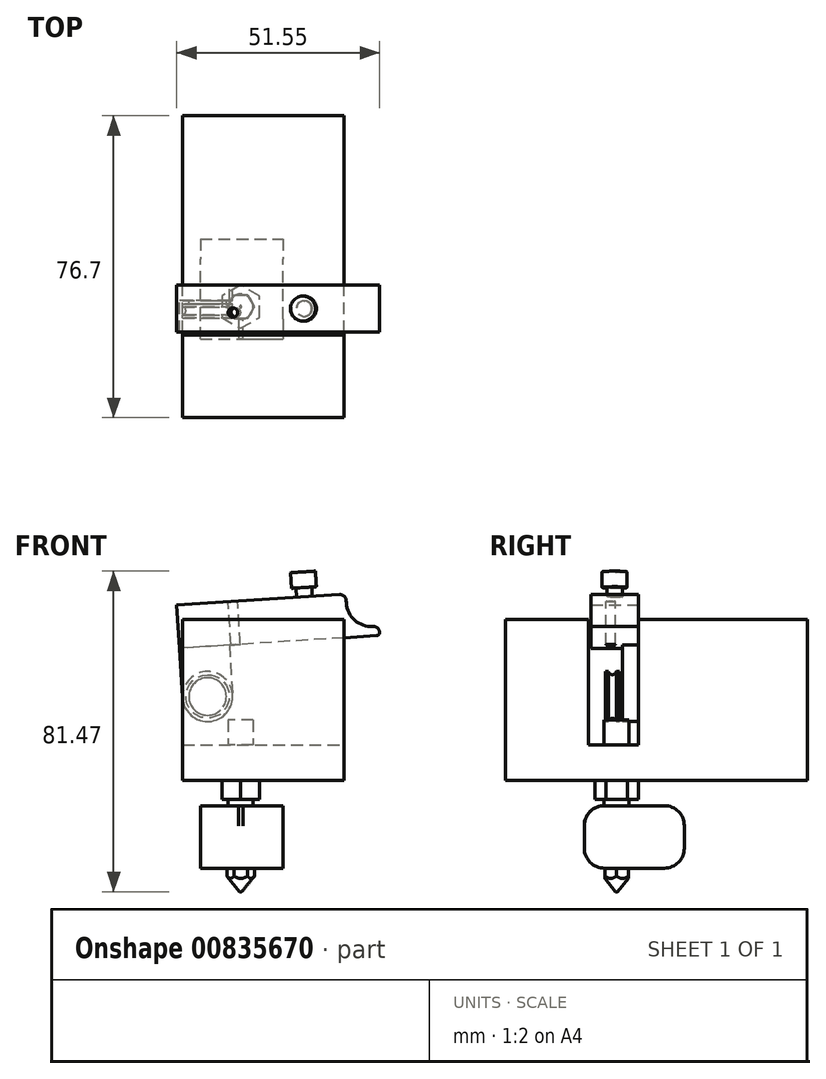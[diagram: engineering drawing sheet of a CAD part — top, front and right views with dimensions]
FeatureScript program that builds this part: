
annotation { "Feature Type Name" : "Feature", "Feature Type Description" : "" }
export const myFeature = defineFeature(function(context is Context, id is Id, definition is map)
    precondition{}
    {
        {
            var Q0;
            Q0=qCreatedBy(makeId("Front.planeOp"),FACE);
            var sketch = newSketch(context, id + "F0", { "sketchPlane" : qUnion([Q0])});
            skLineSegment(sketch, "E0.bottom", {"start": v(-20.5, 20.5) * mm, "end": v(20.5, 20.5) * mm});
            skLineSegment(sketch, "E0.top", {"start": v(-20.5, -20.5) * mm, "end": v(20.5, -20.5) * mm});
            skLineSegment(sketch, "E0.left", {"start": v(-20.5, 20.5) * mm, "end": v(-20.5, -20.5) * mm});
            skLineSegment(sketch, "E0.right", {"start": v(20.5, 20.5) * mm, "end": v(20.5, -20.5) * mm});
            skSolve(sketch);
        }
        {
            var Q0;
            Q0 = qSketchRegion(id + "F0", true);
            extrude(context, id + "F1", {"entities" : qUnion([Q0]), "depth" : 43 * mm, "offsetDistance" : 25.4 * mm});
        }
        {
            var Q0;
            Q0=makeQuery(id+"F1.opExtrude","CAP_FACE",FACE,{"disambiguationData":[OSD([sQuery(id+"F0.wireOp",EDGE,"E0.bottom"),sQuery(id+"F0.wireOp",EDGE,"E0.top"),sQuery(id+"F0.wireOp",EDGE,"E0.left"),sQuery(id+"F0.wireOp",EDGE,"E0.right")])],"isStart":false});
            var sketch = newSketch(context, id + "F2", { "sketchPlane" : qUnion([Q0])});
            skLineSegment(sketch, "E1.bottom", {"start": v(-20.5, -11.5) * mm, "end": v(20.5, -11.5) * mm});
            skLineSegment(sketch, "E1.top", {"start": v(-20.5, -20.5) * mm, "end": v(20.5, -20.5) * mm});
            skLineSegment(sketch, "E1.left", {"start": v(-20.5, -11.5) * mm, "end": v(-20.5, -20.5) * mm});
            skLineSegment(sketch, "E1.right", {"start": v(20.5, -11.5) * mm, "end": v(20.5, -20.5) * mm});
            skSolve(sketch);
        }
        {
            var Q0;
            Q0 = qSketchRegion(id + "F2", true);
            extrude(context, id + "F3", {"entities" : qUnion([Q0]), "operationType" : NewBodyOperationType.ADD, "depth" : 12.7 * mm, "offsetDistance" : 25.4 * mm});
        }
        {
            var Q0;
            Q0=makeQuery(id+"F1.opExtrude","CAP_FACE",FACE,{"disambiguationData":[OSD([sQuery(id+"F0.wireOp",EDGE,"E0.bottom"),sQuery(id+"F0.wireOp",EDGE,"E0.top"),sQuery(id+"F0.wireOp",EDGE,"E0.left"),sQuery(id+"F0.wireOp",EDGE,"E0.right")])],"isStart":false});
            var sketch = newSketch(context, id + "F4", { "sketchPlane" : qUnion([Q0])});
            skLineSegment(sketch, "E2", {"start": v(-20.49, 0.44) * mm, "end": v(-22, 24.1) * mm});
            skLineSegment(sketch, "E3", {"start": v(-22, 24.1) * mm, "end": v(20.96, 26.85) * mm});
            skLineSegment(sketch, "E4", {"start": v(20.96, 26.85) * mm, "end": v(21.5, 18.26) * mm});
            skLineSegment(sketch, "E5", {"start": v(21.5, 18.26) * mm, "end": v(29.44, 18.76) * mm});
            skLineSegment(sketch, "E6", {"start": v(29.44, 18.76) * mm, "end": v(29.6, 16.38) * mm});
            skLineSegment(sketch, "E7", {"start": v(29.6, 16.38) * mm, "end": v(-8.63, 13.93) * mm});
            skLineSegment(sketch, "E8", {"start": v(-8.63, 13.93) * mm, "end": v(-7.81, 1.26) * mm});
            skArc(sketch, "E9", {"start": v(-20.49, 0.44) * mm, "mid": v(-13.74, -5.49) * mm, "end": v(-7.81, 1.26) * mm});
            skSolve(sketch);
        }
        {
            var Q0;
            Q0 = qSketchRegion(id + "F4", true);
            extrude(context, id + "F5", {"entities" : qUnion([Q0]), "operationType" : NewBodyOperationType.ADD, "depth" : 4 * mm, "offsetDistance" : 25.4 * mm});
        }
        {
            var Q0;
            Q0=makeQuery(id+"F5.opExtrude","SWEPT_EDGE",EDGE,{"disambiguationData":[OSD([sQuery(id+"F4.wireOp",EDGE,"E4"),sQuery(id+"F4.wireOp",EDGE,"E5")])]});
            fillet(context, id + "F6", {"entities" : qUnion([Q0]), "radius" : 6.35 * mm, "tangentPropagation" : true, "allowEdgeOverflow" : false});
        }
        {
            var Q0;
            Q0=makeQuery(id+"F5.opExtrude","SWEPT_EDGE",EDGE,{"disambiguationData":[OSD([sQuery(id+"F4.wireOp",EDGE,"E5"),sQuery(id+"F4.wireOp",EDGE,"E6")])]});
            fillet(context, id + "F7", {"entities" : qUnion([Q0]), "radius" : 1.6 * mm, "tangentPropagation" : true, "allowEdgeOverflow" : false});
        }
        {
            var Q0;
            Q0=makeQuery(id+"F5.opExtrude","SWEPT_EDGE",EDGE,{"disambiguationData":[OSD([sQuery(id+"F4.wireOp",EDGE,"E3"),sQuery(id+"F4.wireOp",EDGE,"E4")])]});
            fillet(context, id + "F8", {"entities" : qUnion([Q0]), "radius" : 1.6 * mm, "tangentPropagation" : true, "allowEdgeOverflow" : false});
        }
        {
            var Q0;
            Q0=makeQuery(id+"F5.opExtrude","SWEPT_EDGE",EDGE,{"disambiguationData":[OSD([sQuery(id+"F4.wireOp",EDGE,"E6"),sQuery(id+"F4.wireOp",EDGE,"E7")])]});
            fillet(context, id + "F9", {"entities" : qUnion([Q0]), "radius" : 0.79 * mm, "tangentPropagation" : true, "allowEdgeOverflow" : false});
        }
        {
            var Q0;
            Q0=makeQuery(id+"F5.opExtrude","CAP_FACE",FACE,{"disambiguationData":[OSD([sQuery(id+"F4.wireOp",EDGE,"E2"),sQuery(id+"F4.wireOp",EDGE,"E3"),sQuery(id+"F4.wireOp",EDGE,"E4"),sQuery(id+"F4.wireOp",EDGE,"E5"),sQuery(id+"F4.wireOp",EDGE,"E6"),sQuery(id+"F4.wireOp",EDGE,"E7"),sQuery(id+"F4.wireOp",EDGE,"E8"),sQuery(id+"F4.wireOp",EDGE,"E9")])],"isStart":false});
            var sketch = newSketch(context, id + "F10", { "sketchPlane" : qUnion([Q0])});
            skLineSegment(sketch, "E10.0", {"start": v(-22, 24.1) * mm, "end": v(19.36, 26.75) * mm});
            skArc(sketch, "E10.1", {"start": v(21.06, 25.25) * mm, "mid": v(20.52, 26.35) * mm, "end": v(19.36, 26.75) * mm});
            skLineSegment(sketch, "E10.2", {"start": v(21.06, 25.25) * mm, "end": v(21.1, 24.6) * mm});
            skArc(sketch, "E10.3", {"start": v(27.85, 18.66) * mm, "mid": v(23.25, 20.23) * mm, "end": v(21.1, 24.6) * mm});
            skArc(sketch, "E10.4", {"start": v(29.55, 17.17) * mm, "mid": v(29, 18.27) * mm, "end": v(27.85, 18.66) * mm});
            skArc(sketch, "E10.5", {"start": v(28.8, 16.33) * mm, "mid": v(29.35, 16.6) * mm, "end": v(29.55, 17.17) * mm});
            skLineSegment(sketch, "E10.6", {"start": v(28.8, 16.33) * mm, "end": v(-8.63, 13.93) * mm});
            skLineSegment(sketch, "E11", {"start": v(-8.63, 13.93) * mm, "end": v(-21.3, 13.12) * mm});
            skLineSegment(sketch, "E12", {"start": v(-22, 24.1) * mm, "end": v(-21.3, 13.12) * mm});
            skSolve(sketch);
        }
        {
            var Q0;
            Q0 = qSketchRegion(id + "F10", true);
            extrude(context, id + "F11", {"entities" : qUnion([Q0]), "operationType" : NewBodyOperationType.ADD, "depth" : 8 * mm, "offsetDistance" : 25.4 * mm});
        }
        {
            var Q0;
            Q0=makeQuery(id+"F3.opExtrude","CAP_FACE",FACE,{"disambiguationData":[OSD([sQuery(id+"F2.wireOp",EDGE,"E1.bottom"),sQuery(id+"F2.wireOp",EDGE,"E1.top"),sQuery(id+"F2.wireOp",EDGE,"E1.left"),sQuery(id+"F2.wireOp",EDGE,"E1.right")])],"isStart":false});
            var sketch = newSketch(context, id + "F12", { "sketchPlane" : qUnion([Q0])});
            skLineSegment(sketch, "E13.0.0", {"start": v(-20.5, -20.5) * mm, "end": v(-20.5, 20.5) * mm});
            skLineSegment(sketch, "E13.0.1", {"start": v(-20.5, 20.5) * mm, "end": v(20.5, 20.5) * mm});
            skLineSegment(sketch, "E13.0.2", {"start": v(20.5, 20.5) * mm, "end": v(20.5, -20.5) * mm});
            skLineSegment(sketch, "E13.0.3", {"start": v(20.5, -20.5) * mm, "end": v(-20.5, -20.5) * mm});
            skSolve(sketch);
        }
        {
            var Q0;
            Q0 = qSketchRegion(id + "F12", true);
            extrude(context, id + "F13", {"entities" : qUnion([Q0]), "operationType" : NewBodyOperationType.ADD, "depth" : 21 * mm, "offsetDistance" : 25.4 * mm});
        }
        {
            var Q0;
            Q0=makeQuery(id+"F11.boolean.opBoolean","MERGE",FACE,{"derivedFrom":[makeQuery(id+"F5.opExtrude","SWEPT_FACE",FACE,{"disambiguationData":[OSD([sQuery(id+"F4.wireOp",EDGE,"E3")])]}),makeQuery(id+"F11.opExtrude","SWEPT_FACE",FACE,{"disambiguationData":[OSD([sQuery(id+"F10.wireOp",EDGE,"E10.0")])]})]});
            var sketch = newSketch(context, id + "F14", { "sketchPlane" : qUnion([Q0])});
            skPoint(sketch, "E14", {"position": v(-6.12, -50) * mm});
            skSolve(sketch);
        }
        {
            var Q0;
            Q0=sQuery(id+"F14.wireOp",VERTEX,"E14");
            var Q1;
            Q1=makeQuery(id+"F1.opExtrude","SWEPT_BODY",BODY,{"disambiguationData":[OSD([sQuery(id+"F0.wireOp",EDGE,"E0.bottom"),sQuery(id+"F0.wireOp",EDGE,"E0.top"),sQuery(id+"F0.wireOp",EDGE,"E0.left"),sQuery(id+"F0.wireOp",EDGE,"E0.right")])]});
            hole(context, id + "F15", {"style" : HoleStyle.SIMPLE, "endStyle" : HoleEndStyle.BLIND, "holeDiameter" : 2.4 * mm, "majorDiameter" : 6.35 * mm, "holeDepth" : 12.7 * mm, "isTappedThrough" : true, "tappedDepth" : 12.7 * mm, "tapClearance" : 3, "startFromSketch" : true, "locations" : qUnion([Q0]), "scope" : qUnion([Q1])});
        }
        {
            var Q0;
            Q0=makeQuery(id+"F11.boolean.opBoolean","MERGE",FACE,{"derivedFrom":[makeQuery(id+"F5.opExtrude","SWEPT_FACE",FACE,{"disambiguationData":[OSD([sQuery(id+"F4.wireOp",EDGE,"E3")])]}),makeQuery(id+"F11.opExtrude","SWEPT_FACE",FACE,{"disambiguationData":[OSD([sQuery(id+"F10.wireOp",EDGE,"E10.0")])]})]});
            var sketch = newSketch(context, id + "F16", { "sketchPlane" : qUnion([Q0])});
            skCircle(sketch, "E15", {"center": v(12.12, -49) * mm, "radius": 1.98 * mm});
            skSolve(sketch);
        }
        {
            var Q0;
            Q0 = qSketchRegion(id + "F16", true);
            extrude(context, id + "F17", {"entities" : qUnion([Q0]), "operationType" : NewBodyOperationType.ADD, "depth" : 2.4 * mm, "offsetDistance" : 25.4 * mm});
        }
        {
            var Q0;
            Q0=makeQuery(id+"F17.opExtrude","CAP_FACE",FACE,{"disambiguationData":[OSD([sQuery(id+"F16.wireOp",EDGE,"E15")])],"isStart":false});
            var sketch = newSketch(context, id + "F18", { "sketchPlane" : qUnion([Q0])});
            skCircle(sketch, "E16.0", {"center": v(12.12, -49) * mm, "radius": 1.98 * mm, "construction": true});
            skCircle(sketch, "E17", {"center": v(12.12, -49) * mm, "radius": 3.18 * mm});
            skSolve(sketch);
        }
        {
            var Q0;
            Q0 = qSketchRegion(id + "F18", true);
            extrude(context, id + "F19", {"entities" : qUnion([Q0]), "operationType" : NewBodyOperationType.ADD, "depth" : 3.96 * mm, "offsetDistance" : 25.4 * mm});
        }
        {
            var Q0;
            Q0=makeQuery(id+"F13.boolean.opBoolean","MERGE",FACE,{"derivedFrom":[makeQuery(id+"F3.boolean.opBoolean","MERGE",FACE,{"derivedFrom":[makeQuery(id+"F1.opExtrude","SWEPT_FACE",FACE,{"disambiguationData":[OSD([sQuery(id+"F0.wireOp",EDGE,"E0.top")])]}),makeQuery(id+"F3.opExtrude","SWEPT_FACE",FACE,{"disambiguationData":[OSD([sQuery(id+"F2.wireOp",EDGE,"E1.top")])]})]}),makeQuery(id+"F13.opExtrude","SWEPT_FACE",FACE,{"disambiguationData":[OSD([sQuery(id+"F12.wireOp",EDGE,"E13.0.3")])]})]});
            var sketch = newSketch(context, id + "F20", { "sketchPlane" : qUnion([Q0])});
            skCircle(sketch, "E18.cCircle", {"center": v(-5.74, 48.5) * mm, "radius": 4.76 * mm, "construction": true});
            skLineSegment(sketch, "E18.0", {"start": v(-0.98, 45.75) * mm, "end": v(-5.74, 43) * mm});
            skLineSegment(sketch, "E18.1", {"start": v(-5.74, 43) * mm, "end": v(-10.5, 45.75) * mm});
            skLineSegment(sketch, "E18.2", {"start": v(-10.5, 45.75) * mm, "end": v(-10.5, 51.25) * mm});
            skLineSegment(sketch, "E18.3", {"start": v(-10.5, 51.25) * mm, "end": v(-5.74, 54) * mm});
            skLineSegment(sketch, "E18.4", {"start": v(-5.74, 54) * mm, "end": v(-0.97, 51.25) * mm});
            skLineSegment(sketch, "E18.5", {"start": v(-0.97, 51.25) * mm, "end": v(-0.97, 45.75) * mm});
            skPoint(sketch, "E18.0.midPoint", {"position": v(-3.36, 44.37) * mm});
            skSolve(sketch);
        }
        {
            var Q0;
            Q0 = qSketchRegion(id + "F20", true);
            extrude(context, id + "F21", {"entities" : qUnion([Q0]), "operationType" : NewBodyOperationType.ADD, "depth" : 4.78 * mm, "offsetDistance" : 25.4 * mm});
        }
        {
            var Q0;
            Q0=makeQuery(id+"F21.opExtrude","CAP_FACE",FACE,{"disambiguationData":[OSD([sQuery(id+"F20.wireOp",EDGE,"E18.0"),sQuery(id+"F20.wireOp",EDGE,"E18.1"),sQuery(id+"F20.wireOp",EDGE,"E18.2"),sQuery(id+"F20.wireOp",EDGE,"E18.3"),sQuery(id+"F20.wireOp",EDGE,"E18.4"),sQuery(id+"F20.wireOp",EDGE,"E18.5")])],"isStart":false});
            cPlane(context, id + "F22", {"entities" : qUnion([Q0]), "cplaneType" : CPlaneType.OFFSET, "offset" : 1.6 * mm, "width" : 152.4 * mm, "height" : 152.4 * mm});
        }
        {
            var Q0;
            Q0=qCreatedBy(id+"F22.planeOp",FACE);
            var sketch = newSketch(context, id + "F23", { "sketchPlane" : qUnion([Q0])});
            skLineSegment(sketch, "E19.0.0", {"start": v(-0.97, 45.75) * mm, "end": v(-0.97, 51.25) * mm, "construction": true});
            skLineSegment(sketch, "E19.0.1", {"start": v(-0.98, 51.25) * mm, "end": v(-5.74, 54) * mm, "construction": true});
            skLineSegment(sketch, "E19.0.2", {"start": v(-5.74, 54) * mm, "end": v(-10.5, 51.25) * mm, "construction": true});
            skLineSegment(sketch, "E19.0.3", {"start": v(-10.5, 51.25) * mm, "end": v(-10.5, 45.75) * mm, "construction": true});
            skLineSegment(sketch, "E19.0.4", {"start": v(-10.5, 45.75) * mm, "end": v(-5.74, 43) * mm, "construction": true});
            skLineSegment(sketch, "E19.0.5", {"start": v(-5.74, 43) * mm, "end": v(-0.98, 45.75) * mm, "construction": true});
            skCircle(sketch, "E20", {"center": v(-5.74, 48.5) * mm, "radius": 4.76 * mm, "construction": true});
            skCircle(sketch, "E21", {"center": v(-5.74, 48.5) * mm, "radius": 3.18 * mm});
            skSolve(sketch);
        }
        {
            var Q0;
            Q0 = qSketchRegion(id + "F23", true);
            var Q1;
            Q1=makeQuery(id+"F3.opExtrude","SWEPT_FACE",FACE,{"disambiguationData":[OSD([sQuery(id+"F2.wireOp",EDGE,"E1.bottom")])]});
            extrude(context, id + "F24", {"entities" : qUnion([Q0]), "operationType" : NewBodyOperationType.ADD, "endBound" : BoundingType.UP_TO_SURFACE, "oppositeDirection" : true, "depth" : 25.4 * mm, "endBoundEntityFace" : qUnion([Q1]), "hasOffset" : true, "offsetDistance" : 6.35 * mm, "offsetOppositeDirection" : true});
        }
        {
            var Q0;
            Q0=makeQuery(id+"F5.opExtrude","SWEPT_FACE",FACE,{"disambiguationData":[OSD([sQuery(id+"F4.wireOp",EDGE,"E9")])]});
            var Q1;
            Q1=qCreatedBy(makeId("Right.planeOp"),FACE);
            cPlane(context, id + "F25", {"entities" : qUnion([Q0, Q1]), "cplaneType" : CPlaneType.LINE_ANGLE, "offset" : 25.4 * mm, "angle" : 0 * degree, "width" : 152.4 * mm, "height" : 152.4 * mm});
        }
        {
            var Q0;
            Q0=qCreatedBy(id+"F25.planeOp",FACE);
            var sketch = newSketch(context, id + "F26", { "sketchPlane" : qUnion([Q0])});
            skLineSegment(sketch, "E22", {"start": v(47, 5.61) * mm, "end": v(47.79, 5.61) * mm});
            skLineSegment(sketch, "E23", {"start": v(47.79, 5.61) * mm, "end": v(47.79, 7.21) * mm});
            skLineSegment(sketch, "E24", {"start": v(47.79, 7.21) * mm, "end": v(48.57, 7.21) * mm});
            skLineSegment(sketch, "E25", {"start": v(50.58, 7.21) * mm, "end": v(51.37, 7.21) * mm});
            skLineSegment(sketch, "E26", {"start": v(51.37, 7.21) * mm, "end": v(51.37, 0.86) * mm});
            skLineSegment(sketch, "E27", {"start": v(47, 0.86) * mm, "end": v(47, 5.61) * mm});
            skArc(sketch, "E28", {"start": v(48.57, 7.21) * mm, "mid": v(49.58, 6.4) * mm, "end": v(50.58, 7.21) * mm});
            skLineSegment(sketch, "E29", {"start": v(47, 0.86) * mm, "end": v(51.37, 0.86) * mm});
            skSolve(sketch);
        }
        {
            var Q0;
            Q0 = qSketchRegion(id + "F26", true);
            var Q1;
            Q1=sQuery(id+"F26.wireOp",EDGE,"E29");
            revolve(context, id + "F27", {"operationType" : NewBodyOperationType.ADD, "surfaceOperationType" : NewSurfaceOperationType.NEW, "entities" : qUnion([Q0]), "axis" : qUnion([Q1]), "revolveType" : RevolveType.FULL});
        }
        {
            var Q0;
            Q0=makeQuery(id+"F24.opExtrude","CAP_FACE",FACE,{"disambiguationData":[OSD([sQuery(id+"F23.wireOp",EDGE,"E21")])],"isStart":true});
            var sketch = newSketch(context, id + "F28", { "sketchPlane" : qUnion([Q0])});
            skLineSegment(sketch, "E30.bottom", {"start": v(-16, 56.7) * mm, "end": v(5, 56.7) * mm});
            skLineSegment(sketch, "E30.top", {"start": v(-16, 31.3) * mm, "end": v(5, 31.3) * mm});
            skLineSegment(sketch, "E30.left", {"start": v(-16, 56.7) * mm, "end": v(-16, 31.3) * mm});
            skLineSegment(sketch, "E30.right", {"start": v(5, 56.7) * mm, "end": v(5, 31.3) * mm});
            skSolve(sketch);
        }
        {
            var Q0;
            Q0 = qSketchRegion(id + "F28", true);
            extrude(context, id + "F29", {"entities" : qUnion([Q0]), "operationType" : NewBodyOperationType.ADD, "depth" : 15.88 * mm, "offsetDistance" : 25.4 * mm});
        }
        {
            var Q0;
            Q0=makeQuery(id+"F29.opExtrude","CAP_EDGE",EDGE,{"disambiguationData":[OSD([sQuery(id+"F28.wireOp",EDGE,"E30.bottom")])],"isStart":false});
            var Q1;
            Q1=makeQuery(id+"F29.opExtrude","CAP_EDGE",EDGE,{"disambiguationData":[OSD([sQuery(id+"F28.wireOp",EDGE,"E30.bottom")])],"isStart":true});
            var Q2;
            Q2=makeQuery(id+"F29.opExtrude","CAP_EDGE",EDGE,{"disambiguationData":[OSD([sQuery(id+"F28.wireOp",EDGE,"E30.top")])],"isStart":false});
            var Q3;
            Q3=makeQuery(id+"F29.opExtrude","CAP_EDGE",EDGE,{"disambiguationData":[OSD([sQuery(id+"F28.wireOp",EDGE,"E30.top")])],"isStart":true});
            fillet(context, id + "F30", {"entities" : qUnion([Q0, Q1, Q2, Q3]), "radius" : 5.08 * mm, "tangentPropagation" : true, "allowEdgeOverflow" : false});
        }
        {
            var Q0;
            Q0=makeQuery(id+"F29.opExtrude","CAP_FACE",FACE,{"disambiguationData":[OSD([sQuery(id+"F28.wireOp",EDGE,"E30.bottom"),sQuery(id+"F28.wireOp",EDGE,"E30.top"),sQuery(id+"F28.wireOp",EDGE,"E30.left"),sQuery(id+"F28.wireOp",EDGE,"E30.right")])],"isStart":false});
            var sketch = newSketch(context, id + "F31", { "sketchPlane" : qUnion([Q0])});
            skCircle(sketch, "E31.0", {"center": v(-5.74, 48.5) * mm, "radius": 3.18 * mm, "construction": true});
            skCircle(sketch, "E32.cCircle", {"center": v(-5.74, 48.5) * mm, "radius": 3 * mm, "construction": true});
            skLineSegment(sketch, "E32.0", {"start": v(-2.27, 48.5) * mm, "end": v(-4, 45.5) * mm});
            skLineSegment(sketch, "E32.1", {"start": v(-4, 45.5) * mm, "end": v(-7.47, 45.5) * mm});
            skLineSegment(sketch, "E32.2", {"start": v(-7.47, 45.5) * mm, "end": v(-9.2, 48.5) * mm});
            skLineSegment(sketch, "E32.3", {"start": v(-9.2, 48.5) * mm, "end": v(-7.47, 51.5) * mm});
            skLineSegment(sketch, "E32.4", {"start": v(-7.47, 51.5) * mm, "end": v(-4, 51.5) * mm});
            skLineSegment(sketch, "E32.5", {"start": v(-4, 51.5) * mm, "end": v(-2.27, 48.5) * mm});
            skPoint(sketch, "E32.0.midPoint", {"position": v(-3.14, 47) * mm});
            skSolve(sketch);
        }
        {
            var Q0;
            Q0 = qSketchRegion(id + "F31", true);
            extrude(context, id + "F32", {"entities" : qUnion([Q0]), "operationType" : NewBodyOperationType.ADD, "depth" : 6 * mm, "offsetDistance" : 25.4 * mm});
        }
        {
            var Q0;
            Q0=makeQuery(id+"F32.opExtrude","SWEPT_FACE",FACE,{"disambiguationData":[OSD([sQuery(id+"F31.wireOp",EDGE,"E32.4")])]});
            cPlane(context, id + "F33", {"entities" : qUnion([Q0]), "cplaneType" : CPlaneType.OFFSET, "offset" : 3 * mm, "oppositeDirection" : true, "width" : 152.4 * mm, "height" : 152.4 * mm});
        }
        {
            var Q0;
            Q0=qCreatedBy(id+"F33.planeOp",FACE);
            var sketch = newSketch(context, id + "F34", { "sketchPlane" : qUnion([Q0])});
            skLineSegment(sketch, "E33", {"start": v(-5.49, -48.75) * mm, "end": v(-2.25, -44.75) * mm});
            skLineSegment(sketch, "E34", {"start": v(-2.25, -44.75) * mm, "end": v(-2.25, -48.75) * mm});
            skLineSegment(sketch, "E35", {"start": v(-2.25, -48.75) * mm, "end": v(-5.49, -48.75) * mm});
            skLineSegment(sketch, "E36", {"start": v(-5.74, -48.75) * mm, "end": v(-5.74, -46.14) * mm, "construction": true});
            skSolve(sketch);
        }
        {
            var Q0;
            Q0 = qSketchRegion(id + "F34", true);
            var Q1;
            Q1=sQuery(id+"F34.wireOp",EDGE,"E36");
            revolve(context, id + "F35", {"operationType" : NewBodyOperationType.REMOVE, "surfaceOperationType" : NewSurfaceOperationType.NEW, "entities" : qUnion([Q0]), "axis" : qUnion([Q1]), "revolveType" : RevolveType.FULL, "oppositeDirection" : true});
        }
    });
